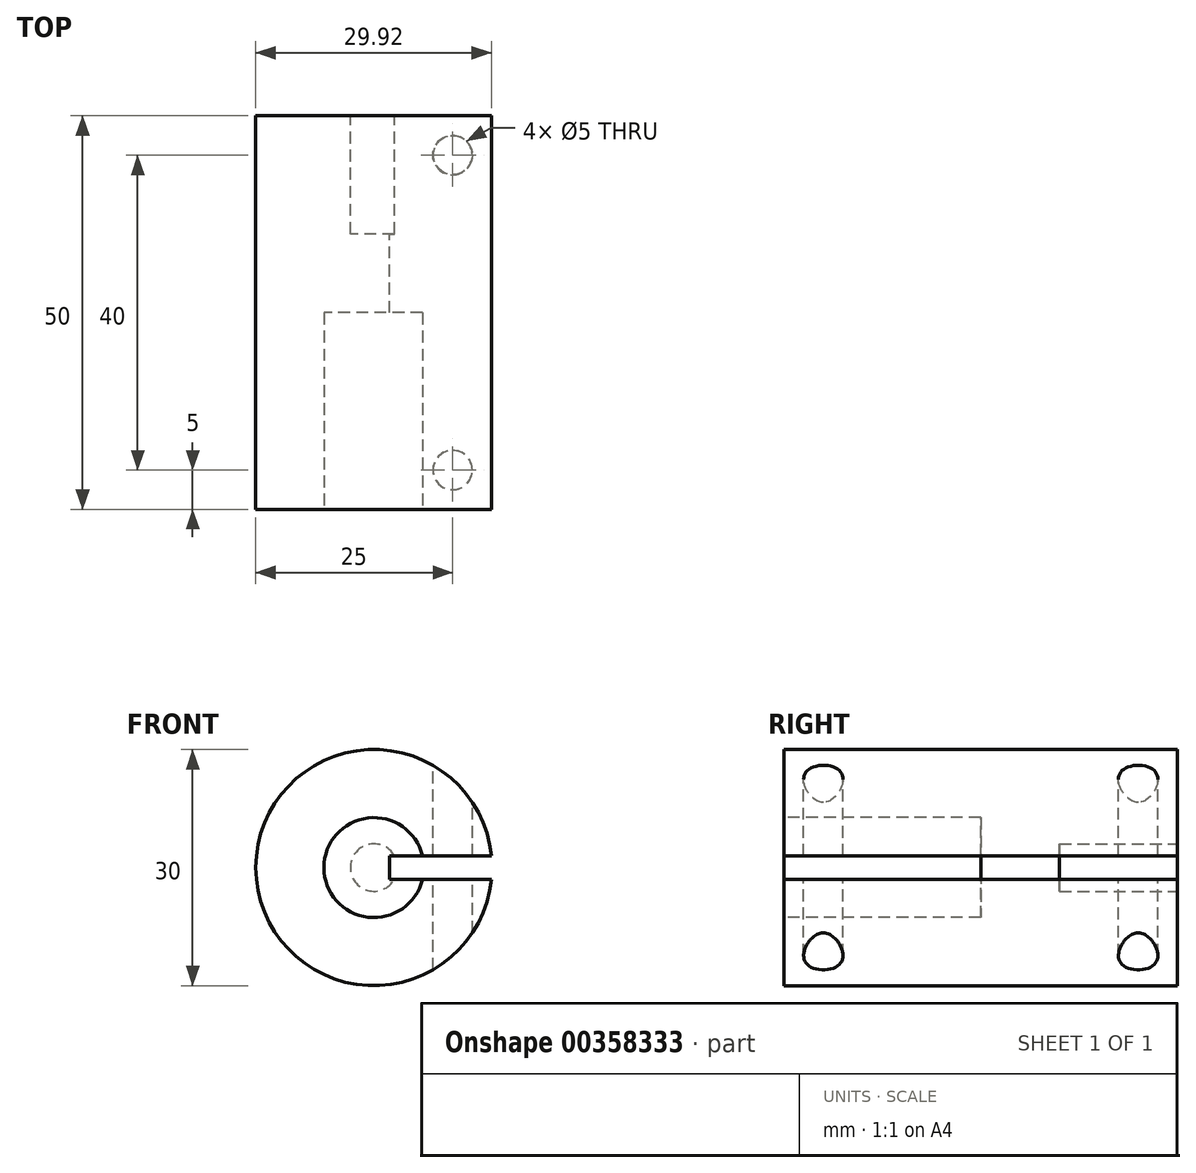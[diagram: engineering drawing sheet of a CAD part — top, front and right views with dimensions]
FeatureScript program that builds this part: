
annotation { "Feature Type Name" : "Feature", "Feature Type Description" : "" }
export const myFeature = defineFeature(function(context is Context, id is Id, definition is map)
    precondition{}
    {
        {
            var Q0;
            Q0=qCreatedBy(makeId("Front.planeOp"),FACE);
            var sketch = newSketch(context, id + "F0", { "sketchPlane" : qUnion([Q0])});
            skCircle(sketch, "E0", {"center": v(0, 0) * mm, "radius": 15 * mm});
            skSolve(sketch);
        }
        {
            var Q0;
            Q0 = qSketchRegion(id + "F0", true);
            extrude(context, id + "F1", {"entities" : qUnion([Q0]), "depth" : 50 * mm});
        }
        {
            var Q0;
            Q0=makeQuery(id+"F1.opExtrude","CAP_FACE",FACE,{"disambiguationData":[OSD([sQuery(id+"F0.wireOp",EDGE,"E0")])],"isStart":false});
            var sketch = newSketch(context, id + "F2", { "sketchPlane" : qUnion([Q0])});
            skCircle(sketch, "E1", {"center": v(0, 0) * mm, "radius": 6.35 * mm});
            skSolve(sketch);
        }
        {
            var Q0;
            Q0 = qSketchRegion(id + "F2", true);
            extrude(context, id + "F3", {"entities" : qUnion([Q0]), "operationType" : NewBodyOperationType.REMOVE, "oppositeDirection" : true, "depth" : 25 * mm});
        }
        {
            var Q0;
            Q0=makeQuery(id+"F1.opExtrude","CAP_FACE",FACE,{"disambiguationData":[OSD([sQuery(id+"F0.wireOp",EDGE,"E0")])],"isStart":true});
            var sketch = newSketch(context, id + "F4", { "sketchPlane" : qUnion([Q0])});
            skCircle(sketch, "E2", {"center": v(0, 0) * mm, "radius": 3 * mm});
            skSolve(sketch);
        }
        {
            var Q0;
            Q0 = qSketchRegion(id + "F4", true);
            extrude(context, id + "F5", {"entities" : qUnion([Q0]), "operationType" : NewBodyOperationType.REMOVE, "oppositeDirection" : true, "depth" : 15 * mm});
        }
        {
            var Q0;
            Q0=makeQuery(id+"F1.opExtrude","CAP_FACE",FACE,{"disambiguationData":[OSD([sQuery(id+"F0.wireOp",EDGE,"E0")])],"isStart":true});
            var sketch = newSketch(context, id + "F6", { "sketchPlane" : qUnion([Q0])});
            skLineSegment(sketch, "E3.bottom", {"start": v(-2, 1.5) * mm, "end": v(-15, 1.5) * mm});
            skLineSegment(sketch, "E3.top", {"start": v(-2, -1.5) * mm, "end": v(-15, -1.5) * mm});
            skLineSegment(sketch, "E3.left", {"start": v(-2, 1.5) * mm, "end": v(-2, -1.5) * mm});
            skLineSegment(sketch, "E3.right", {"start": v(-15, 1.5) * mm, "end": v(-15, -1.5) * mm});
            skPoint(sketch, "E4", {"position": v(-2, 0) * mm});
            skSolve(sketch);
        }
        {
            var Q0;
            Q0 = qSketchRegion(id + "F6", true);
            extrude(context, id + "F7", {"entities" : qUnion([Q0]), "operationType" : NewBodyOperationType.REMOVE, "endBound" : BoundingType.THROUGH_ALL, "oppositeDirection" : true, "depth" : 25 * mm});
        }
        {
            var Q0;
            Q0=qCreatedBy(makeId("Top.planeOp"),FACE);
            var sketch = newSketch(context, id + "F8", { "sketchPlane" : qUnion([Q0])});
            skCircle(sketch, "E5", {"center": v(10, -5) * mm, "radius": 2.5 * mm});
            skCircle(sketch, "E6", {"center": v(10, -45) * mm, "radius": 2.5 * mm});
            skSolve(sketch);
        }
        {
            var Q0;
            Q0 = qSketchRegion(id + "F8", true);
            extrude(context, id + "F9", {"entities" : qUnion([Q0]), "operationType" : NewBodyOperationType.REMOVE, "endBound" : BoundingType.THROUGH_ALL, "oppositeDirection" : true, "depth" : 25 * mm, "hasSecondDirection" : true, "secondDirectionBound" : BoundingType.THROUGH_ALL, "secondDirectionOppositeDirection" : false, "secondDirectionDepth" : 25 * mm});
        }
    });
